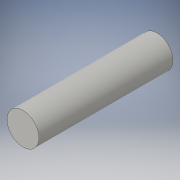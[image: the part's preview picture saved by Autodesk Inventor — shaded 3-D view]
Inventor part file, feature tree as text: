
AUTODESK INVENTOR PART (.ipt)
format: ipt  version: 2016 (Build 200138000, 138)  size: 84,992 bytes
history: native  units: in
note: dims shown in document units (in); Inventor stores cm internally (conversion verified against a paired STEP export)
features: extrude x1, sketch x1
ambient origin geometry x8: Origin, YZ Plane, XZ Plane, XY Plane, X Axis, Y Axis, Z Axis, Center Point
bodies: Solid1 (feature_tree)
feature tree (2):
  extrude  "Extrusion1"  Depth=3.2795in TaperAngle=0.0deg
  sketch  "Sketch1"  dims[d0=0.7795in d1=3.2795in d2=0.0in]
